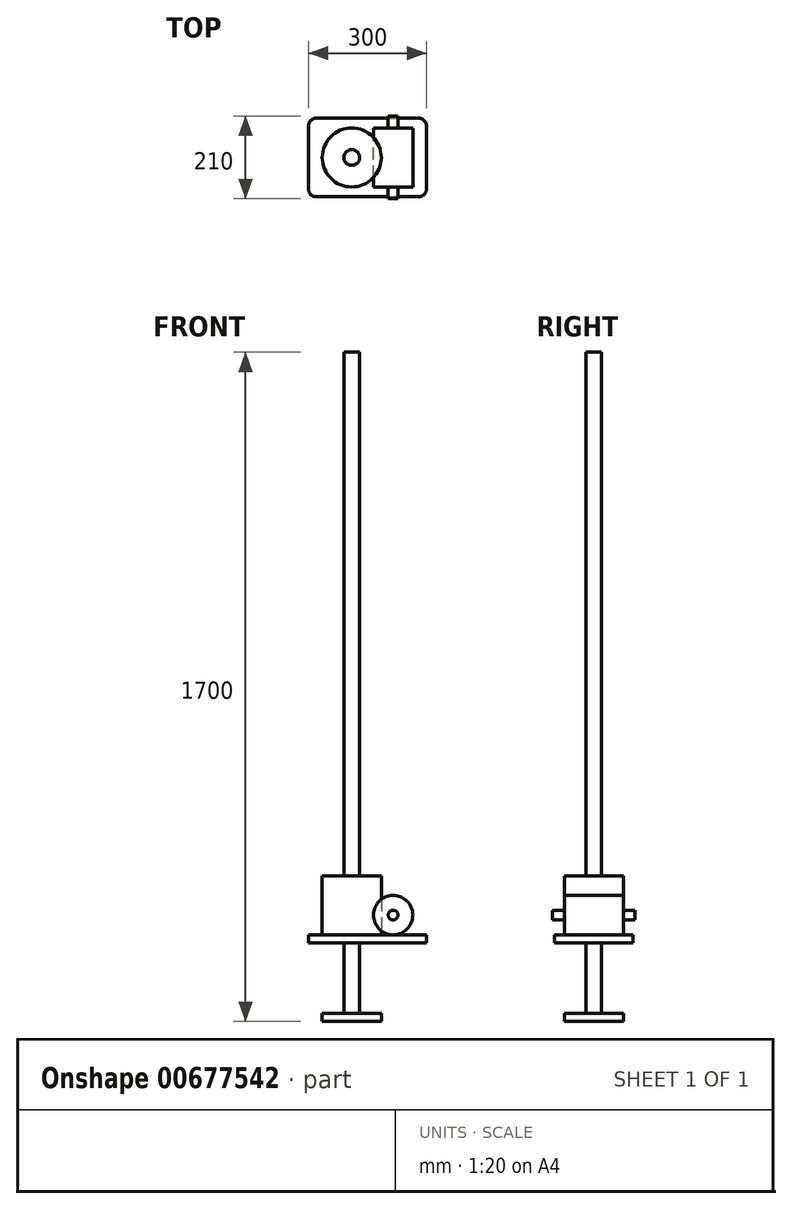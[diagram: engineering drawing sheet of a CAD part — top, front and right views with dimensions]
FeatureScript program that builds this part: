
annotation { "Feature Type Name" : "Feature", "Feature Type Description" : "" }
export const myFeature = defineFeature(function(context is Context, id is Id, definition is map)
    precondition{}
    {
        {
            var Q0;
            Q0=qCreatedBy(makeId("Top.planeOp"),FACE);
            var sketch = newSketch(context, id + "F0", { "sketchPlane" : qUnion([Q0])});
            skLineSegment(sketch, "E0.bottom", {"start": v(-150, -100) * mm, "end": v(150, -100) * mm});
            skLineSegment(sketch, "E0.top", {"start": v(-150, 100) * mm, "end": v(150, 100) * mm});
            skLineSegment(sketch, "E0.left", {"start": v(-150, -100) * mm, "end": v(-150, 100) * mm});
            skLineSegment(sketch, "E0.right", {"start": v(150, -100) * mm, "end": v(150, 100) * mm});
            skPoint(sketch, "E0.middle", {"position": v(0, 0) * mm});
            skSolve(sketch);
        }
        {
            var Q0;
            Q0 = qSketchRegion(id + "F0", true);
            extrude(context, id + "F1", {"entities" : qUnion([Q0]), "depth" : 20 * mm, "offsetDistance" : 25 * mm});
        }
        {
            var Q0;
            Q0=makeQuery(id+"F1.opExtrude","CAP_FACE",FACE,{"disambiguationData":[OSD([sQuery(id+"F0.wireOp",EDGE,"E0.bottom"),sQuery(id+"F0.wireOp",EDGE,"E0.top"),sQuery(id+"F0.wireOp",EDGE,"E0.left"),sQuery(id+"F0.wireOp",EDGE,"E0.right")])],"isStart":false});
            var sketch = newSketch(context, id + "F2", { "sketchPlane" : qUnion([Q0])});
            skCircle(sketch, "E1", {"center": v(-40, 0) * mm, "radius": 75 * mm});
            skSolve(sketch);
        }
        {
            var Q0;
            Q0=makeQuery(id+"F2.imprint","IMPRINT",FACE,{"disambiguationData":[TD([[makeQuery(id+"F2.imprint","IMPRINT",EDGE,{"derivedFrom":sQuery(id+"F2.wireOp",EDGE,"E1")}),1.0]])]});
            extrude(context, id + "F3", {"entities" : qUnion([Q0]), "operationType" : NewBodyOperationType.ADD, "depth" : 150 * mm, "offsetDistance" : 25 * mm});
        }
        {
            var Q0;
            Q0=qCreatedBy(makeId("Front.planeOp"),FACE);
            var sketch = newSketch(context, id + "F4", { "sketchPlane" : qUnion([Q0])});
            skCircle(sketch, "E2", {"center": v(65.07, 70) * mm, "radius": 50 * mm});
            skSolve(sketch);
        }
        {
            var Q0;
            Q0=makeQuery(id+"F4.imprint","IMPRINT",FACE,{"disambiguationData":[TD([[makeQuery(id+"F4.imprint","IMPRINT",EDGE,{"derivedFrom":sQuery(id+"F4.wireOp",EDGE,"E2")}),1.0]])]});
            extrude(context, id + "F5", {"entities" : qUnion([Q0]), "endBound" : BoundingType.SYMMETRIC, "depth" : 150 * mm, "offsetDistance" : 25 * mm});
        }
        {
            var Q0;
            Q0=makeQuery(id+"F5.opExtrude","CAP_FACE",FACE,{"disambiguationData":[OSD([sQuery(id+"F4.wireOp",EDGE,"E2")])],"isStart":false});
            var sketch = newSketch(context, id + "F6", { "sketchPlane" : qUnion([Q0])});
            skCircle(sketch, "E3", {"center": v(65.07, 70) * mm, "radius": 12.5 * mm});
            skSolve(sketch);
        }
        {
            var Q0;
            Q0=makeQuery(id+"F6.imprint","IMPRINT",FACE,{"disambiguationData":[TD([[makeQuery(id+"F6.imprint","IMPRINT",EDGE,{"derivedFrom":sQuery(id+"F6.wireOp",EDGE,"E3")}),1.0]])]});
            var Q1;
            Q1=sQuery(id+"F6.wireOp",EDGE,"E3");
            extrude(context, id + "F7", {"entities" : qUnion([Q0]), "operationType" : NewBodyOperationType.ADD, "surfaceEntities" : qUnion([Q1]), "depth" : 30 * mm, "offsetDistance" : 25 * mm, "hasSecondDirection" : true, "secondDirectionOppositeDirection" : true, "secondDirectionDepth" : 180 * mm});
        }
        {
            var Q0;
            Q0=makeQuery(id+"F1.opExtrude","CAP_FACE",FACE,{"disambiguationData":[OSD([sQuery(id+"F0.wireOp",EDGE,"E0.bottom"),sQuery(id+"F0.wireOp",EDGE,"E0.top"),sQuery(id+"F0.wireOp",EDGE,"E0.left"),sQuery(id+"F0.wireOp",EDGE,"E0.right")])],"isStart":true});
            var sketch = newSketch(context, id + "F8", { "sketchPlane" : qUnion([Q0])});
            skCircle(sketch, "E4", {"center": v(-40, 0) * mm, "radius": 20 * mm});
            skSolve(sketch);
        }
        {
            var Q0;
            Q0=makeQuery(id+"F8.imprint","IMPRINT",FACE,{"disambiguationData":[TD([[makeQuery(id+"F8.imprint","IMPRINT",EDGE,{"derivedFrom":sQuery(id+"F8.wireOp",EDGE,"E4")}),1.0]])]});
            var Q1;
            Q1=sQuery(id+"F8.wireOp",EDGE,"E4");
            extrude(context, id + "F9", {"entities" : qUnion([Q0]), "operationType" : NewBodyOperationType.ADD, "surfaceEntities" : qUnion([Q1]), "depth" : 200 * mm, "offsetDistance" : 25 * mm, "hasSecondDirection" : true, "secondDirectionOppositeDirection" : true, "secondDirectionDepth" : 1500 * mm});
        }
        {
            var Q0;
            Q0=makeQuery(id+"F9.opExtrude","CAP_FACE",FACE,{"disambiguationData":[OSD([sQuery(id+"F8.wireOp",EDGE,"E4")])],"isStart":false});
            var sketch = newSketch(context, id + "F10", { "sketchPlane" : qUnion([Q0])});
            skCircle(sketch, "E5", {"center": v(-40, 0) * mm, "radius": 75 * mm});
            skSolve(sketch);
        }
        {
            var Q0;
            Q0 = qSketchRegion(id + "F10", true);
            extrude(context, id + "F11", {"entities" : qUnion([Q0]), "operationType" : NewBodyOperationType.ADD, "oppositeDirection" : true, "depth" : 20 * mm, "offsetDistance" : 25 * mm});
        }
        {
            var Q0;
            Q0=makeQuery(id+"F1.opExtrude","SWEPT_EDGE",EDGE,{"disambiguationData":[OSD([sQuery(id+"F0.wireOp",EDGE,"E0.top"),sQuery(id+"F0.wireOp",EDGE,"E0.right")])]});
            var Q1;
            Q1=makeQuery(id+"F1.opExtrude","SWEPT_EDGE",EDGE,{"disambiguationData":[OSD([sQuery(id+"F0.wireOp",EDGE,"E0.bottom"),sQuery(id+"F0.wireOp",EDGE,"E0.right")])]});
            var Q2;
            Q2=makeQuery(id+"F1.opExtrude","SWEPT_EDGE",EDGE,{"disambiguationData":[OSD([sQuery(id+"F0.wireOp",EDGE,"E0.bottom"),sQuery(id+"F0.wireOp",EDGE,"E0.left")])]});
            var Q3;
            Q3=makeQuery(id+"F1.opExtrude","SWEPT_EDGE",EDGE,{"disambiguationData":[OSD([sQuery(id+"F0.wireOp",EDGE,"E0.top"),sQuery(id+"F0.wireOp",EDGE,"E0.left")])]});
            fillet(context, id + "F12", {"entities" : qUnion([Q0, Q1, Q2, Q3]), "radius" : 20 * mm, "tangentPropagation" : true, "allowEdgeOverflow" : false});
        }
    });
